# Revit family: Reece_Shower_Kado_Lux_Shower System_Angled
name_source: partatom
category: Plumbing Fixtures
revit_build: Autodesk Revit 2018 (Build: 20190510_1515(x64)
units: mm (PartAtom-declared; Revit-internal decimal feet)

## family parameters
Always vertical = Yes
Cut with Voids When Loaded = Yes
Part Type = Normal
Room Calculation Point = Yes
Round Connector Dimension = Use Diameter
Shared = Yes
Work Plane-Based = Yes

## types (1)
- Angled_1000 mm x 1000 mm_Rear Outlet_Chrome
    Default Elevation = 0 mm  [stored 0 ft]
    Description = Kado Lux Shower System Angled 1000mm x 1000mm Rear Outlet Chrome
    Disclaimer = THIS FILE IS THE PROPERTY OF THE REECE GROUP. IT MAY NOT BE REPRODUCED, REVERSE-ENGINEERED OR MODIFIED. ANY REPUBLICATION, TRANSMISSION OR DISTRIBUTION FOR THE PURPOSE OF COMMERCIALLY EXPLOITING THE FILES IS PROHIBITED.
    Keynote = Product #9506232, Reece_Shower_Kado_Lux_Shower System_Angled - Angled_1000 mm x 1000 mm_Rear Outlet_Chrome
    Manufacturer = Kado
    Model = Lux
    Reece_Detail_Additional = Shower System
    Reece_Detail_Disclaimer = THIS FILE IS THE PROPERTY OF THE REECE GROUP. IT MAY NOT BE REPRODUCED, REVERSE-ENGINEERED OR MODIFIED. ANY REPUBLICATION, TRANSMISSION OR DISTRIBUTION FOR THE PURPOSE OF COMMERCIALLY EXPLOITING THE FILES IS PROHIBITED.
    Reece_Material_Base = Reece_Acrylic_White
    Reece_Material_Main = Reece_Brass_Chrome
    Reece_Material_Screen = Reece_Safety Glass_Transparent
    Reece_Material_Secondary = Reece_Plastic_Transparent
    Reece_Overall_Depth = 1000 mm  [stored 3.28084 ft]
    Reece_Overall_Height = 2060 mm  [stored 6.75853 ft]
    Reece_Overall_Width = 1000 mm  [stored 3.28084 ft]
    Reece_Product_Brand = Kado
    Reece_Product_Description = Kado Lux Shower System Angled 1000mm x 1000mm Rear Outlet Chrome
    Reece_Product_Mount = Floor Mounted
    Reece_Product_Number = 9506232
    Reece_Product_Sub Brand = Lux
    Reece_Product_Type = Shower
    Reece_Product_Web Page = https://www.reece.com.au
    Reece_Screen_Height = 2000 mm  [stored 6.56168 ft]
    Type Comments = Shower
    URL = https://www.reece.com.au

note: [stored X ft] marks values corroborated as IEEE doubles in the binary element streams (Revit-internal decimal feet)

## geometry (parser evidence)
native form markers: Sweep x8
no freeform markers — native parametric forms only
